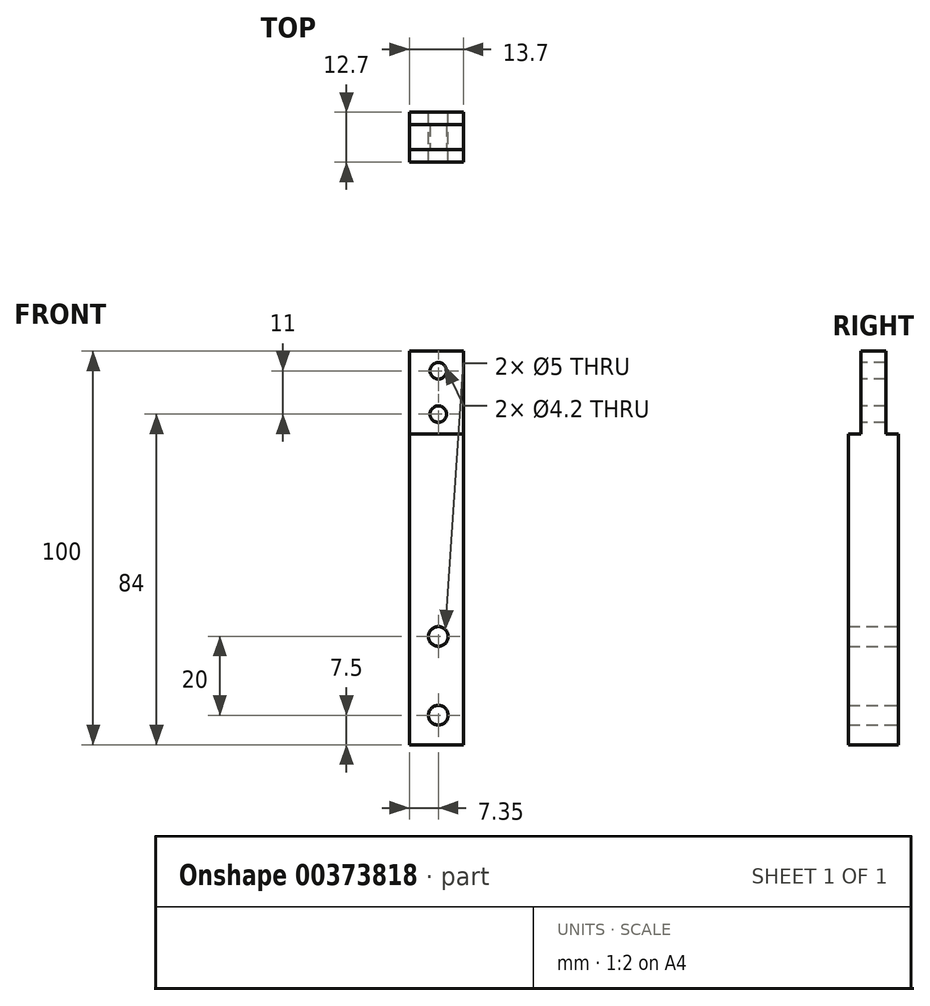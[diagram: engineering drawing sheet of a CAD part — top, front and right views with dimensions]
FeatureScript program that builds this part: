
annotation { "Feature Type Name" : "Feature", "Feature Type Description" : "" }
export const myFeature = defineFeature(function(context is Context, id is Id, definition is map)
    precondition{}
    {
        {
            var Q0;
            Q0=qCreatedBy(makeId("Front.planeOp"),FACE);
            var sketch = newSketch(context, id + "F0", { "sketchPlane" : qUnion([Q0])});
            skLineSegment(sketch, "E0.bottom", {"start": v(-6.35, -50) * mm, "end": v(6.35, -50) * mm});
            skLineSegment(sketch, "E0.top", {"start": v(-6.35, 50) * mm, "end": v(6.35, 50) * mm});
            skLineSegment(sketch, "E0.left", {"start": v(-6.35, -50) * mm, "end": v(-6.35, 50) * mm});
            skLineSegment(sketch, "E0.right", {"start": v(6.35, -50) * mm, "end": v(6.35, 50) * mm});
            skPoint(sketch, "E0.middle", {"position": v(0, 0) * mm});
            skCircle(sketch, "E1", {"center": v(0, -42.5) * mm, "radius": 2.5 * mm});
            skCircle(sketch, "E2", {"center": v(0, -22.5) * mm, "radius": 2.5 * mm});
            skSolve(sketch);
        }
        {
            var Q0;
            Q0=makeQuery(id+"F0.imprint","IMPRINT",FACE,{"disambiguationData":[TD([[makeQuery(id+"F0.imprint","IMPRINT",EDGE,{"derivedFrom":sQuery(id+"F0.wireOp",EDGE,"E0.bottom")}),1.0]])]});
            extrude(context, id + "F1", {"entities" : qUnion([Q0]), "depth" : 12.7 * mm});
        }
        {
            var Q0;
            Q0=makeQuery(id+"F1.opExtrude","CAP_FACE",FACE,{"disambiguationData":[OSD([sQuery(id+"F0.wireOp",EDGE,"E0.bottom"),sQuery(id+"F0.wireOp",EDGE,"E0.top"),sQuery(id+"F0.wireOp",EDGE,"E0.left"),sQuery(id+"F0.wireOp",EDGE,"E0.right"),sQuery(id+"F0.wireOp",EDGE,"E1"),sQuery(id+"F0.wireOp",EDGE,"E2")])],"isStart":false});
            var sketch = newSketch(context, id + "F2", { "sketchPlane" : qUnion([Q0])});
            skPoint(sketch, "E3", {"position": v(0, 45) * mm});
            skPoint(sketch, "E4", {"position": v(0, 34) * mm});
            skSolve(sketch);
        }
        {
            var Q0;
            Q0=sQuery(id+"F2.wireOp",VERTEX,"E3");
            var Q1;
            Q1=sQuery(id+"F2.wireOp",VERTEX,"E4");
            var Q2;
            Q2=makeQuery(id+"F1.opExtrude","SWEPT_BODY",BODY,{"disambiguationData":[OSD([sQuery(id+"F0.wireOp",EDGE,"E0.bottom"),sQuery(id+"F0.wireOp",EDGE,"E0.top"),sQuery(id+"F0.wireOp",EDGE,"E0.left"),sQuery(id+"F0.wireOp",EDGE,"E0.right"),sQuery(id+"F0.wireOp",EDGE,"E1"),sQuery(id+"F0.wireOp",EDGE,"E2")])]});
            hole(context, id + "F3", {"style" : HoleStyle.SIMPLE, "endStyle" : HoleEndStyle.THROUGH, "standardTappedOrClearance" : lookupTablePath({ "standard" : "ISO", "engagement" : "75%", "pitch" : "0.8 mm", "size" : "M5", "type" : "Tapped" }), "standardBlindInLast" : lookupTablePath({ "standard" : "ISO", "engagement" : "75%", "pitch" : "0.8 mm", "size" : "M5", "type" : "Tapped" }), "holeDiameter" : 4.2 * mm, "showTappedDepth" : true, "isTappedThrough" : true, "tappedDepth" : 2.4 * mm, "tapClearance" : 8, "startFromSketch" : true, "locations" : qUnion([Q0, Q1]), "scope" : qUnion([Q2]), "majorDiameter" : 5 * mm});
        }
        {
            var Q0;
            Q0=makeQuery(id+"F1.opExtrude","SWEPT_FACE",FACE,{"disambiguationData":[OSD([sQuery(id+"F0.wireOp",EDGE,"E0.left")])]});
            var sketch = newSketch(context, id + "F4", { "sketchPlane" : qUnion([Q0])});
            skLineSegment(sketch, "E5.bottom", {"start": v(3.17, 50) * mm, "end": v(9.52, 50) * mm});
            skLineSegment(sketch, "E5.left", {"start": v(3.17, 50) * mm, "end": v(3.17, 29) * mm});
            skLineSegment(sketch, "E5.right", {"start": v(9.52, 50) * mm, "end": v(9.52, 29) * mm});
            skPoint(sketch, "E5.middle", {"position": v(6.35, 39.5) * mm});
            skPoint(sketch, "E5.middle.positionSnap0", {"position": v(6.35, 50) * mm});
            skPoint(sketch, "E5.centerSnap0", {"position": v(6.35, 50) * mm});
            skLineSegment(sketch, "E6", {"start": v(0, 29) * mm, "end": v(3.17, 29) * mm});
            skLineSegment(sketch, "E7.trimOffspring", {"start": v(9.52, 29) * mm, "end": v(12.7, 29) * mm});
            skSolve(sketch);
        }
        {
            var Q0;
            {var subQ0=sQuery(id+"F4.wireOp",EDGE,"E5.left");Q0=makeQuery(id+"F4.imprint","IMPRINT",FACE,{"disambiguationData":[TD([[makeQuery(id+"F4.imprint","IMPRINT",EDGE,{"derivedFrom":subQ0}),-1.0]])]});}
            var Q1;
            {var subQ0=sQuery(id+"F4.wireOp",EDGE,"E5.right");Q1=makeQuery(id+"F4.imprint","IMPRINT",FACE,{"disambiguationData":[TD([[makeQuery(id+"F4.imprint","IMPRINT",EDGE,{"derivedFrom":subQ0}),1.0]])]});}
            extrude(context, id + "F5", {"entities" : qUnion([Q0, Q1]), "operationType" : NewBodyOperationType.REMOVE, "endBound" : BoundingType.THROUGH_ALL, "oppositeDirection" : true, "depth" : 25 * mm});
        }
        {
            var Q0;
            Q0=makeQuery(id+"F1.opExtrude","SWEPT_FACE",FACE,{"disambiguationData":[OSD([sQuery(id+"F0.wireOp",EDGE,"E0.left")])]});
            extrude(context, id + "F6", {"entities" : qUnion([Q0]), "operationType" : NewBodyOperationType.ADD, "depth" : 1 * mm});
        }
    });
